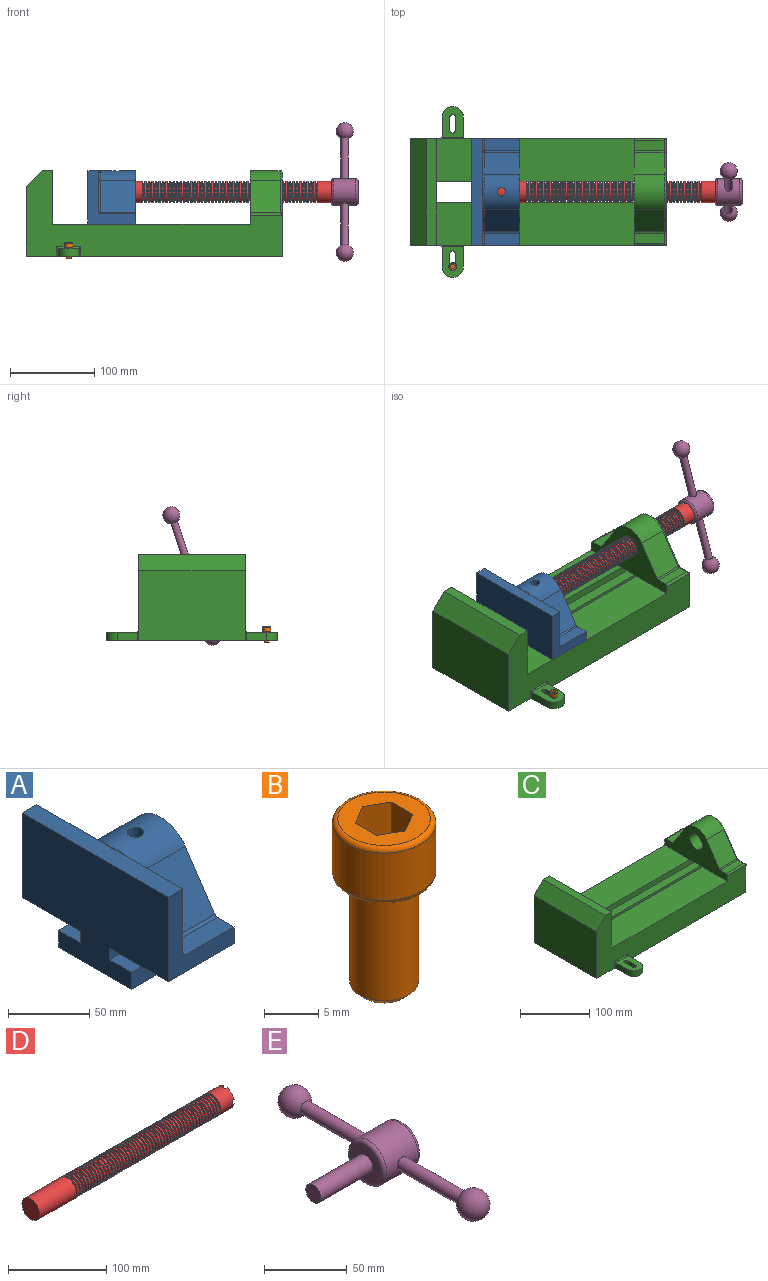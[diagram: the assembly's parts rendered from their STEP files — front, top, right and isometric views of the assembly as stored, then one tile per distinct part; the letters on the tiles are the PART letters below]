
ASSEMBLY  parts=5 mates=5
PART A: 36 faces, bbox 57.2x127x89 mm
  f0: plane 57.15x50.8mm, normal (0,0,-1), area 2903.2mm2, adj f6,f9,f10,f23
  f1: cylinder r=12.7mm len=44.45mm, axis (1,0,0), area 3464.3mm2, adj f6,f15,f16
  f2: plane 41.91x14.52mm, normal (0,0,1), area 608.5mm2, adj f6,f11,f24,f25
  f3: plane 51.86x48.26mm, normal (1,0,0), area 1495.7mm2, adj f8,f10,f31,f33,f35
  f4: plane 51.86x48.26mm, normal (1,0,0), area 1495.7mm2, adj f8,f11,f24,f28,f29
  f5: plane 57.15x50.8mm, normal (0,0,-1), area 2903.2mm2, adj f6,f9,f11,f22
  f6: plane 127x85.09mm, normal (1,0,0), area 5190.6mm2, adj f0,f1,f2,f5,f7,f10,f11,f12
  f7: plane 41.91x14.52mm, normal (0,0,1), area 608.5mm2, adj f6,f10,f30,f31
  f8: plane 127x12.7mm, normal (0,0,1), area 1612.9mm2, adj f3,f4,f9,f10,f11,f26,f34
  f9: plane 127x85.09mm, normal (-1,0,0), area 9096.8mm2, adj f0,f5,f8,f10,f11,f17,f18,f19
  f10: plane 63.5x57.15mm, normal (0,-1,0), area 1372.3mm2, adj f0,f3,f6,f7,f8,f9,f31
  f11: plane 63.5x57.15mm, normal (0,1,0), area 1372.3mm2, adj f2,f4,f5,f6,f8,f9,f24
  f12: plane 41.91x38.43mm, normal (0,-0.83,0.56), area 1939.2mm2, adj f6,f13,f30,f33
  f13: cylinder r=25.4mm len=44.45mm, axis (1,0,0), area 2026.5mm2, adj f6,f12,f14,f16,f26,f28,f34,f35
  f14: plane 41.91x38.43mm, normal (0,0.83,0.56), area 1939.2mm2, adj f6,f13,f25,f29
  f15: plane 25.4x25.4mm, normal (1,0,0), area 506.7mm2, adj f1
  f16: cylinder r=5.08mm len=13.76mm, axis (0,0,1), area 414mm2, adj f1,f13
  f17: plane 57.15x19.05mm, normal (0,0,1), area 1088.7mm2, adj f6,f9,f18,f23
  f18: plane 57.15x12.7mm, normal (0,-1,0), area 725.8mm2, adj f6,f9,f17,f19
  f19: plane 63.5x57.15mm, normal (0,0,-1), area 3629mm2, adj f6,f9,f18,f20
  f20: plane 57.15x12.7mm, normal (0,1,0), area 725.8mm2, adj f6,f9,f19,f21
  f21: plane 57.15x19.05mm, normal (0,0,1), area 1088.7mm2, adj f6,f9,f20,f22
  f22: plane 57.15x8.89mm, normal (0,1,0), area 508.1mm2, adj f5,f6,f9,f21
  f23: plane 57.15x8.89mm, normal (0,-1,0), area 508.1mm2, adj f0,f6,f9,f17
  f24: cylinder r=2.54mm len=14.52mm, axis (0,-1,0), area 57.9mm2, adj f2,f4,f11,f27
  f25: cylinder r=2.54mm len=41.91mm, axis (1,0,0), area 104.3mm2, adj f2,f6,f14,f27
  f26: bspline ~12.24x2.8mm, area 20.9mm2, adj f8,f13,f28
  f27: sphere r=2.54mm, area 6.3mm2, adj f24,f25,f29
  f28: torus R=27.94mm, axis (1,0,0), area 57.8mm2, adj f4,f13,f26,f29
  f29: cylinder r=2.54mm len=39.84mm, axis (0,-0.56,0.83), area 184.6mm2, adj f4,f14,f27,f28
  f30: cylinder r=2.54mm len=41.91mm, axis (1,0,0), area 104.3mm2, adj f6,f7,f12,f32
  f31: cylinder r=2.54mm len=14.52mm, axis (0,-1,0), area 57.9mm2, adj f3,f7,f10,f32
  f32: sphere r=2.54mm, area 6.3mm2, adj f30,f31,f33
  f33: cylinder r=2.54mm len=39.84mm, axis (0,-0.56,-0.83), area 184.6mm2, adj f3,f12,f32,f35
  f34: bspline ~12.24x2.8mm, area 20.9mm2, adj f8,f13,f35
  f35: torus R=27.94mm, axis (1,0,0), area 57.8mm2, adj f3,f13,f33,f34
PART B: 15 faces, bbox 10.3x10.3x19.1 mm
  f0: plane 8.51x8.51mm, normal (0,0,1), area 37.2mm2, adj f5,f6,f7,f8,f9,f10,f14
  f1: cylinder r=3.17mm len=11.94mm, axis (0,0,1), area 238.2mm2, adj f4,f12
  f2: plane 4.83x4.83mm, normal (0,0,-1), area 18.3mm2, adj f12
  f3: cylinder r=4.76mm len=9.53mm, axis (0,0,-1), area 159.6mm2, adj f13,f14
  f4: plane 8.51x8.51mm, normal (0,0,-1), area 25.2mm2, adj f1,f13
  f5: plane 4.83x2.38mm, normal (-0.5,-0.87,0), area 13.3mm2, adj f0,f6,f10,f11
  f6: plane 4.83x2.38mm, normal (0.5,-0.87,0), area 13.3mm2, adj f0,f5,f7,f11
  f7: plane 4.83x2.75mm, normal (1,0,0), area 13.3mm2, adj f0,f6,f8,f11
  f8: plane 4.83x2.38mm, normal (0.5,0.87,0), area 13.3mm2, adj f0,f7,f9,f11
  f9: plane 4.83x2.38mm, normal (-0.5,0.87,0), area 13.3mm2, adj f0,f8,f10,f11
  f10: plane 4.83x2.75mm, normal (-1,0,0), area 13.3mm2, adj f0,f5,f9,f11
  f11: plane 5.5x4.76mm, normal (0,0,1), area 19.6mm2, adj f5,f6,f7,f8,f9,f10
  f12: cone r=3.17mm half-angle=45deg, axis (0,0,1), area 18.9mm2, adj f1,f2
  f13: torus R=4.25mm, axis (0,0,1), area 23mm2, adj f3,f4
  f14: torus R=4.25mm, axis (0,0,1), area 23mm2, adj f0,f3
PART C: 61 faces, bbox 304.8x203.2x103.7 mm
  f0: plane 304.8x101.6mm, normal (0,1,0), area 13520.3mm2, adj f3,f4,f5,f6,f7,f8,f9,f16
  f1: plane 304.8x101.6mm, normal (0,-1,0), area 13520.3mm2, adj f2,f3,f5,f6,f7,f8,f9,f16
  f2: plane 234.95x50.8mm, normal (0,0,1), area 11935.5mm2, adj f1,f5,f16,f26
  f3: plane 127x99.06mm, normal (1,0,0), area 7097.5mm2, adj f0,f1,f9,f14,f17,f18,f19,f20
  f4: plane 234.95x50.8mm, normal (0,0,1), area 11935.5mm2, adj f0,f5,f16,f27
  f5: plane 127x101.6mm, normal (1,0,0), area 9516.1mm2, adj f0,f1,f2,f4,f6,f9,f18,f19
  f6: plane 127x12.7mm, normal (0,0,1), area 1612.9mm2, adj f0,f1,f5,f7
  f7: plane 127x19.05mm, normal (-0.71,0,0.71), area 3421.5mm2, adj f0,f1,f6,f8
  f8: plane 127x82.55mm, normal (-1,0,0), area 10483.8mm2, adj f0,f1,f7,f9
  f9: plane 304.8x203.2mm, normal (0,0,-1), area 33298.3mm2, adj f0,f1,f3,f5,f8,f21,f22,f39
  f10: plane 35.56x11.98mm, normal (0,0,1), area 426mm2, adj f16,f28,f29,f30
  f11: plane 38.43x35.56mm, normal (0,0.83,0.56), area 1645.4mm2, adj f12,f16,f29,f32
  f12: cylinder r=25.4mm len=42.19mm, axis (1,0,0), area 1770.2mm2, adj f11,f13,f16,f33
  f13: plane 38.43x35.56mm, normal (0,-0.83,0.56), area 1645.4mm2, adj f12,f16,f34,f35
  f14: cylinder r=12.7mm len=38.1mm, axis (1,0,0), area 3040.2mm2, adj f3,f16
  f15: plane 35.56x11.98mm, normal (0,0,1), area 426mm2, adj f16,f34,f36,f38
  f16: plane 127x63.5mm, normal (-1,0,0), area 4155.5mm2, adj f0,f1,f2,f4,f10,f11,f12,f13
  f17: plane 38.1x25.4mm, normal (0,0,-1), area 967.7mm2, adj f3,f16,f26,f27
  f18: plane 273.05x19.05mm, normal (0,0,-1), area 5201.6mm2, adj f3,f5,f19,f26
  f19: plane 273.05x12.7mm, normal (0,1,0), area 3467.7mm2, adj f3,f5,f18,f20
  f20: plane 273.05x19.05mm, normal (0,0,1), area 5201.6mm2, adj f3,f5,f19,f21
  f21: plane 273.05x16.51mm, normal (0,1,0), area 4508.1mm2, adj f3,f5,f9,f20
  f22: plane 273.05x16.51mm, normal (0,-1,0), area 4508.1mm2, adj f3,f5,f9,f23
  f23: plane 273.05x19.05mm, normal (0,0,1), area 5201.6mm2, adj f3,f5,f22,f24
  f24: plane 273.05x12.7mm, normal (0,-1,0), area 3467.7mm2, adj f3,f5,f23,f25
  f25: plane 273.05x19.05mm, normal (0,0,-1), area 5201.6mm2, adj f3,f5,f24,f27
  f26: plane 273.05x8.89mm, normal (0,1,0), area 2427.4mm2, adj f2,f3,f5,f17,f18
  f27: plane 273.05x8.89mm, normal (0,-1,0), area 2427.4mm2, adj f3,f4,f5,f17,f25
  f28: cylinder r=2.54mm len=38.1mm, axis (1,0,0), area 148.3mm2, adj f0,f10,f16,f30
  f29: cylinder r=2.54mm len=35.56mm, axis (-1,0,0), area 88.5mm2, adj f10,f11,f16,f31
  f30: cylinder r=2.54mm len=14.52mm, axis (0,1,0), area 54.3mm2, adj f3,f10,f28,f31
  f31: torus R=5.08mm, axis (-1,0,0), area 13.5mm2, adj f3,f29,f30,f32
  f32: cylinder r=2.54mm len=39.84mm, axis (0,0.56,-0.83), area 184.6mm2, adj f3,f11,f31,f33
  f33: torus R=22.86mm, axis (-1,0,0), area 191.4mm2, adj f3,f12,f32,f35
  f34: cylinder r=2.54mm len=35.56mm, axis (-1,0,0), area 88.5mm2, adj f13,f15,f16,f37
  f35: cylinder r=2.54mm len=39.84mm, axis (0,0.56,0.83), area 184.6mm2, adj f3,f13,f33,f37
  f36: cylinder r=2.54mm len=38.1mm, axis (-1,0,0), area 148.3mm2, adj f1,f15,f16,f38
  f37: torus R=5.08mm, axis (-1,0,0), area 13.5mm2, adj f3,f34,f35,f38
  f38: cylinder r=2.54mm len=14.52mm, axis (0,1,0), area 54.3mm2, adj f3,f15,f36,f37
  f39: plane 23.88x9.53mm, normal (-1,0,0), area 227.4mm2, adj f9,f45,f46,f60
  f40: plane 23.88x9.53mm, normal (1,0,0), area 227.4mm2, adj f9,f45,f46,f58
  f41: cylinder r=3.3mm len=9.53mm, axis (0,0,-1), area 98.8mm2, adj f9,f42,f44,f46
  f42: plane 15.62x9.53mm, normal (-1,0,0), area 148.8mm2, adj f9,f41,f43,f46
  f43: cylinder r=3.3mm len=9.53mm, axis (0,0,-1), area 98.8mm2, adj f9,f42,f44,f46
  f44: plane 15.62x9.53mm, normal (1,0,0), area 148.8mm2, adj f9,f41,f43,f46
  f45: cylinder r=12.7mm len=25.4mm, axis (0,0,-1), area 380mm2, adj f9,f39,f40,f46
  f46: plane 36.58x25.4mm, normal (0,0,1), area 722.4mm2, adj f39,f40,f41,f42,f43,f44,f45,f59
  f47: plane 23.88x9.53mm, normal (-1,0,0), area 227.4mm2, adj f9,f53,f54,f56
  f48: plane 23.88x9.53mm, normal (1,0,0), area 227.4mm2, adj f9,f53,f54,f55
  f49: cylinder r=3.3mm len=9.53mm, axis (0,0,-1), area 98.8mm2, adj f9,f50,f52,f54
  f50: plane 15.62x9.53mm, normal (-1,0,0), area 148.8mm2, adj f9,f49,f51,f54
  f51: cylinder r=3.3mm len=9.53mm, axis (0,0,-1), area 98.8mm2, adj f9,f50,f52,f54
  f52: plane 15.62x9.53mm, normal (1,0,0), area 148.8mm2, adj f9,f49,f51,f54
  f53: cylinder r=12.7mm len=25.4mm, axis (0,0,-1), area 380mm2, adj f9,f47,f48,f54
  f54: plane 36.58x25.4mm, normal (0,0,1), area 722.4mm2, adj f47,f48,f49,f50,f51,f52,f53,f57
  f55: cylinder r=1.52mm len=11.05mm, axis (0,0,-1), area 24.1mm2, adj f0,f9,f48,f57
  f56: cylinder r=1.52mm len=11.05mm, axis (0,0,1), area 24.1mm2, adj f0,f9,f47,f57
  f57: cylinder r=1.52mm len=28.45mm, axis (1,0,0), area 63.5mm2, adj f0,f54,f55,f56
  f58: cylinder r=1.52mm len=11.05mm, axis (0,0,1), area 24.1mm2, adj f1,f9,f40,f59
  f59: cylinder r=1.52mm len=28.45mm, axis (-1,0,0), area 63.5mm2, adj f1,f46,f58,f60
  f60: cylinder r=1.52mm len=11.05mm, axis (0,0,-1), area 24.1mm2, adj f1,f9,f39,f59
PART D: 220 faces, bbox 279.4x25.4x25.4 mm
  f0: cylinder r=12.7mm len=25.4mm, axis (-1,0,0), area 1468.2mm2, adj f1,f2,f3,f5,f7,f208,f209,f210
  f1: plane 9.9x9.9mm, normal (1,0,0), area 62.3mm2, adj f0,f4,f213,f216
  f2: plane 9.9x9.9mm, normal (1,0,0), area 62.3mm2, adj f0,f4,f210,f218
  f3: plane 9.9x9.9mm, normal (1,0,0), area 62.3mm2, adj f0,f4,f209,f212
  f4: cylinder r=6.35mm len=25.4mm, axis (1,0,0), area 960.3mm2, adj f1,f2,f3,f5,f6,f208,f209,f210
  f5: plane 9.9x9.9mm, normal (1,0,0), area 62.3mm2, adj f0,f4,f215,f217
  f6: plane 12.7x12.7mm, normal (1,0,0), area 126.7mm2, adj f4
  f7: cone r=12.7mm half-angle=76deg, axis (1,0,0), area 188mm2, adj f0,f9
  f8: cone r=10.16mm half-angle=76deg, axis (-1,0,0), area 188mm2, adj f9,f10
  f9: cylinder r=10.16mm len=20.32mm, axis (1,0,0), area 81.1mm2, adj f7,f8
  f10: cylinder r=12.7mm len=25.4mm, axis (-1,0,0), area 131.7mm2, adj f8,f11
  f11: cone r=12.7mm half-angle=76deg, axis (1,0,0), area 188mm2, adj f10,f13
  f12: cone r=10.16mm half-angle=76deg, axis (-1,0,0), area 188mm2, adj f13,f14
  f13: cylinder r=10.16mm len=20.32mm, axis (1,0,0), area 81.1mm2, adj f11,f12
  f14: cylinder r=12.7mm len=25.4mm, axis (-1,0,0), area 131.7mm2, adj f12,f15
  f15: cone r=12.7mm half-angle=76deg, axis (1,0,0), area 188mm2, adj f14,f17
  f16: cone r=10.16mm half-angle=76deg, axis (-1,0,0), area 188mm2, adj f17,f18
  f17: cylinder r=10.16mm len=20.32mm, axis (1,0,0), area 81.1mm2, adj f15,f16
  f18: cylinder r=12.7mm len=25.4mm, axis (-1,0,0), area 131.7mm2, adj f16,f19
  f19: cone r=12.7mm half-angle=76deg, axis (1,0,0), area 188mm2, adj f18,f21
  f20: cone r=10.16mm half-angle=76deg, axis (-1,0,0), area 188mm2, adj f21,f22
  f21: cylinder r=10.16mm len=20.32mm, axis (1,0,0), area 81.1mm2, adj f19,f20
  f22: cylinder r=12.7mm len=25.4mm, axis (-1,0,0), area 131.7mm2, adj f20,f23
  f23: cone r=12.7mm half-angle=76deg, axis (1,0,0), area 188mm2, adj f22,f25
  f24: cone r=10.16mm half-angle=76deg, axis (-1,0,0), area 188mm2, adj f25,f26
  f25: cylinder r=10.16mm len=20.32mm, axis (1,0,0), area 81.1mm2, adj f23,f24
  f26: cylinder r=12.7mm len=25.4mm, axis (-1,0,0), area 131.7mm2, adj f24,f27
  f27: cone r=12.7mm half-angle=76deg, axis (1,0,0), area 188mm2, adj f26,f29
  f28: cone r=10.16mm half-angle=76deg, axis (-1,0,0), area 188mm2, adj f29,f30
  f29: cylinder r=10.16mm len=20.32mm, axis (1,0,0), area 81.1mm2, adj f27,f28
  f30: cylinder r=12.7mm len=25.4mm, axis (-1,0,0), area 131.7mm2, adj f28,f31
  f31: cone r=12.7mm half-angle=76deg, axis (1,0,0), area 188mm2, adj f30,f33
  f32: cone r=10.16mm half-angle=76deg, axis (-1,0,0), area 188mm2, adj f33,f34
  f33: cylinder r=10.16mm len=20.32mm, axis (1,0,0), area 81.1mm2, adj f31,f32
  f34: cylinder r=12.7mm len=25.4mm, axis (-1,0,0), area 131.7mm2, adj f32,f35
  f35: cone r=12.7mm half-angle=76deg, axis (1,0,0), area 188mm2, adj f34,f37
  f36: cone r=10.16mm half-angle=76deg, axis (-1,0,0), area 188mm2, adj f37,f38
  f37: cylinder r=10.16mm len=20.32mm, axis (1,0,0), area 81.1mm2, adj f35,f36
  f38: cylinder r=12.7mm len=25.4mm, axis (-1,0,0), area 131.7mm2, adj f36,f39
  f39: cone r=12.7mm half-angle=76deg, axis (1,0,0), area 188mm2, adj f38,f41
  f40: cone r=10.16mm half-angle=76deg, axis (-1,0,0), area 188mm2, adj f41,f42
  f41: cylinder r=10.16mm len=20.32mm, axis (1,0,0), area 81.1mm2, adj f39,f40
  f42: cylinder r=12.7mm len=25.4mm, axis (-1,0,0), area 131.7mm2, adj f40,f43
  f43: cone r=12.7mm half-angle=76deg, axis (1,0,0), area 188mm2, adj f42,f45
  f44: cone r=10.16mm half-angle=76deg, axis (-1,0,0), area 188mm2, adj f45,f46
  f45: cylinder r=10.16mm len=20.32mm, axis (1,0,0), area 81.1mm2, adj f43,f44
  f46: cylinder r=12.7mm len=25.4mm, axis (-1,0,0), area 131.7mm2, adj f44,f47
  f47: cone r=12.7mm half-angle=76deg, axis (1,0,0), area 188mm2, adj f46,f49
  f48: cone r=10.16mm half-angle=76deg, axis (-1,0,0), area 188mm2, adj f49,f50
  f49: cylinder r=10.16mm len=20.32mm, axis (1,0,0), area 81.1mm2, adj f47,f48
  f50: cylinder r=12.7mm len=25.4mm, axis (-1,0,0), area 131.7mm2, adj f48,f51
  f51: cone r=12.7mm half-angle=76deg, axis (1,0,0), area 188mm2, adj f50,f53
  f52: cone r=10.16mm half-angle=76deg, axis (-1,0,0), area 188mm2, adj f53,f54
  f53: cylinder r=10.16mm len=20.32mm, axis (1,0,0), area 81.1mm2, adj f51,f52
  f54: cylinder r=12.7mm len=25.4mm, axis (-1,0,0), area 131.7mm2, adj f52,f55
  f55: cone r=12.7mm half-angle=76deg, axis (1,0,0), area 188mm2, adj f54,f57
  f56: cone r=10.16mm half-angle=76deg, axis (-1,0,0), area 188mm2, adj f57,f58
  f57: cylinder r=10.16mm len=20.32mm, axis (1,0,0), area 81.1mm2, adj f55,f56
  f58: cylinder r=12.7mm len=25.4mm, axis (-1,0,0), area 131.7mm2, adj f56,f59
  f59: cone r=12.7mm half-angle=76deg, axis (1,0,0), area 188mm2, adj f58,f61
  f60: cone r=10.16mm half-angle=76deg, axis (-1,0,0), area 188mm2, adj f61,f62
  f61: cylinder r=10.16mm len=20.32mm, axis (1,0,0), area 81.1mm2, adj f59,f60
  f62: cylinder r=12.7mm len=25.4mm, axis (-1,0,0), area 131.7mm2, adj f60,f63
  f63: cone r=12.7mm half-angle=76deg, axis (1,0,0), area 188mm2, adj f62,f65
  f64: cone r=10.16mm half-angle=76deg, axis (-1,0,0), area 188mm2, adj f65,f66
  f65: cylinder r=10.16mm len=20.32mm, axis (1,0,0), area 81.1mm2, adj f63,f64
  f66: cylinder r=12.7mm len=25.4mm, axis (-1,0,0), area 131.7mm2, adj f64,f67
  f67: cone r=12.7mm half-angle=76deg, axis (1,0,0), area 188mm2, adj f66,f69
  f68: cone r=10.16mm half-angle=76deg, axis (-1,0,0), area 188mm2, adj f69,f70
  f69: cylinder r=10.16mm len=20.32mm, axis (1,0,0), area 81.1mm2, adj f67,f68
  f70: cylinder r=12.7mm len=25.4mm, axis (-1,0,0), area 131.7mm2, adj f68,f71
  f71: cone r=12.7mm half-angle=76deg, axis (1,0,0), area 188mm2, adj f70,f73
  f72: cone r=10.16mm half-angle=76deg, axis (-1,0,0), area 188mm2, adj f73,f74
  f73: cylinder r=10.16mm len=20.32mm, axis (1,0,0), area 81.1mm2, adj f71,f72
  f74: cylinder r=12.7mm len=25.4mm, axis (-1,0,0), area 131.7mm2, adj f72,f75
  f75: cone r=12.7mm half-angle=76deg, axis (1,0,0), area 188mm2, adj f74,f77
  f76: cone r=10.16mm half-angle=76deg, axis (-1,0,0), area 188mm2, adj f77,f78
  f77: cylinder r=10.16mm len=20.32mm, axis (1,0,0), area 81.1mm2, adj f75,f76
  f78: cylinder r=12.7mm len=25.4mm, axis (-1,0,0), area 131.7mm2, adj f76,f79
  f79: cone r=12.7mm half-angle=76deg, axis (1,0,0), area 188mm2, adj f78,f81
  f80: cone r=10.16mm half-angle=76deg, axis (-1,0,0), area 188mm2, adj f81,f82
  f81: cylinder r=10.16mm len=20.32mm, axis (1,0,0), area 81.1mm2, adj f79,f80
  f82: cylinder r=12.7mm len=25.4mm, axis (-1,0,0), area 131.7mm2, adj f80,f83
  f83: cone r=12.7mm half-angle=76deg, axis (1,0,0), area 188mm2, adj f82,f85
  f84: cone r=10.16mm half-angle=76deg, axis (-1,0,0), area 188mm2, adj f85,f86
  f85: cylinder r=10.16mm len=20.32mm, axis (1,0,0), area 81.1mm2, adj f83,f84
  f86: cylinder r=12.7mm len=25.4mm, axis (-1,0,0), area 131.7mm2, adj f84,f87
  f87: cone r=12.7mm half-angle=76deg, axis (1,0,0), area 188mm2, adj f86,f89
  f88: cone r=10.16mm half-angle=76deg, axis (-1,0,0), area 188mm2, adj f89,f90
  f89: cylinder r=10.16mm len=20.32mm, axis (1,0,0), area 81.1mm2, adj f87,f88
  f90: cylinder r=12.7mm len=25.4mm, axis (-1,0,0), area 131.7mm2, adj f88,f91
  f91: cone r=12.7mm half-angle=76deg, axis (1,0,0), area 188mm2, adj f90,f93
  f92: cone r=10.16mm half-angle=76deg, axis (-1,0,0), area 188mm2, adj f93,f94
  f93: cylinder r=10.16mm len=20.32mm, axis (1,0,0), area 81.1mm2, adj f91,f92
  f94: cylinder r=12.7mm len=25.4mm, axis (-1,0,0), area 131.7mm2, adj f92,f95
  f95: cone r=12.7mm half-angle=76deg, axis (1,0,0), area 188mm2, adj f94,f97
  f96: cone r=10.16mm half-angle=76deg, axis (-1,0,0), area 188mm2, adj f97,f98
  f97: cylinder r=10.16mm len=20.32mm, axis (1,0,0), area 81.1mm2, adj f95,f96
  f98: cylinder r=12.7mm len=25.4mm, axis (-1,0,0), area 131.7mm2, adj f96,f99
  f99: cone r=12.7mm half-angle=76deg, axis (1,0,0), area 188mm2, adj f98,f101
  f100: cone r=10.16mm half-angle=76deg, axis (-1,0,0), area 188mm2, adj f101,f102
  f101: cylinder r=10.16mm len=20.32mm, axis (1,0,0), area 81.1mm2, adj f99,f100
  f102: cylinder r=12.7mm len=25.4mm, axis (-1,0,0), area 131.7mm2, adj f100,f103
  f103: cone r=12.7mm half-angle=76deg, axis (1,0,0), area 188mm2, adj f102,f105
  f104: cone r=10.16mm half-angle=76deg, axis (-1,0,0), area 188mm2, adj f105,f106
  f105: cylinder r=10.16mm len=20.32mm, axis (1,0,0), area 81.1mm2, adj f103,f104
  f106: cylinder r=12.7mm len=25.4mm, axis (-1,0,0), area 131.7mm2, adj f104,f107
  f107: cone r=12.7mm half-angle=76deg, axis (1,0,0), area 188mm2, adj f106,f109
  f108: cone r=10.16mm half-angle=76deg, axis (-1,0,0), area 188mm2, adj f109,f110
  f109: cylinder r=10.16mm len=20.32mm, axis (1,0,0), area 81.1mm2, adj f107,f108
  f110: cylinder r=12.7mm len=25.4mm, axis (-1,0,0), area 131.7mm2, adj f108,f111
  f111: cone r=12.7mm half-angle=76deg, axis (1,0,0), area 188mm2, adj f110,f113
  f112: cone r=10.16mm half-angle=76deg, axis (-1,0,0), area 188mm2, adj f113,f114
  f113: cylinder r=10.16mm len=20.32mm, axis (1,0,0), area 81.1mm2, adj f111,f112
  f114: cylinder r=12.7mm len=25.4mm, axis (-1,0,0), area 131.7mm2, adj f112,f115
  f115: cone r=12.7mm half-angle=76deg, axis (1,0,0), area 188mm2, adj f114,f117
  f116: cone r=10.16mm half-angle=76deg, axis (-1,0,0), area 188mm2, adj f117,f118
  f117: cylinder r=10.16mm len=20.32mm, axis (1,0,0), area 81.1mm2, adj f115,f116
  f118: cylinder r=12.7mm len=25.4mm, axis (-1,0,0), area 131.7mm2, adj f116,f119
  f119: cone r=12.7mm half-angle=76deg, axis (1,0,0), area 188mm2, adj f118,f121
  f120: cone r=10.16mm half-angle=76deg, axis (-1,0,0), area 188mm2, adj f121,f122
  f121: cylinder r=10.16mm len=20.32mm, axis (1,0,0), area 81.1mm2, adj f119,f120
  f122: cylinder r=12.7mm len=25.4mm, axis (-1,0,0), area 131.7mm2, adj f120,f123
  f123: cone r=12.7mm half-angle=76deg, axis (1,0,0), area 188mm2, adj f122,f125
  f124: cone r=10.16mm half-angle=76deg, axis (-1,0,0), area 188mm2, adj f125,f126
  f125: cylinder r=10.16mm len=20.32mm, axis (1,0,0), area 81.1mm2, adj f123,f124
  f126: cylinder r=12.7mm len=25.4mm, axis (-1,0,0), area 131.7mm2, adj f124,f127
  f127: cone r=12.7mm half-angle=76deg, axis (1,0,0), area 188mm2, adj f126,f129
  f128: cone r=10.16mm half-angle=76deg, axis (-1,0,0), area 188mm2, adj f129,f130
  f129: cylinder r=10.16mm len=20.32mm, axis (1,0,0), area 81.1mm2, adj f127,f128
  f130: cylinder r=12.7mm len=25.4mm, axis (-1,0,0), area 131.7mm2, adj f128,f131
  f131: cone r=12.7mm half-angle=76deg, axis (1,0,0), area 188mm2, adj f130,f133
  f132: cone r=10.16mm half-angle=76deg, axis (-1,0,0), area 188mm2, adj f133,f134
  f133: cylinder r=10.16mm len=20.32mm, axis (1,0,0), area 81.1mm2, adj f131,f132
  f134: cylinder r=12.7mm len=25.4mm, axis (-1,0,0), area 131.7mm2, adj f132,f135
  f135: cone r=12.7mm half-angle=76deg, axis (1,0,0), area 188mm2, adj f134,f137
  f136: cone r=10.16mm half-angle=76deg, axis (-1,0,0), area 188mm2, adj f137,f138
  f137: cylinder r=10.16mm len=20.32mm, axis (1,0,0), area 81.1mm2, adj f135,f136
  f138: cylinder r=12.7mm len=25.4mm, axis (-1,0,0), area 131.7mm2, adj f136,f139
  f139: cone r=12.7mm half-angle=76deg, axis (1,0,0), area 188mm2, adj f138,f141
  f140: cone r=10.16mm half-angle=76deg, axis (-1,0,0), area 188mm2, adj f141,f142
  f141: cylinder r=10.16mm len=20.32mm, axis (1,0,0), area 81.1mm2, adj f139,f140
  f142: cylinder r=12.7mm len=25.4mm, axis (-1,0,0), area 131.7mm2, adj f140,f143
  f143: cone r=12.7mm half-angle=76deg, axis (1,0,0), area 188mm2, adj f142,f145
  f144: cone r=10.16mm half-angle=76deg, axis (-1,0,0), area 188mm2, adj f145,f146
  f145: cylinder r=10.16mm len=20.32mm, axis (1,0,0), area 81.1mm2, adj f143,f144
  f146: cylinder r=12.7mm len=25.4mm, axis (-1,0,0), area 131.7mm2, adj f144,f147
  f147: cone r=12.7mm half-angle=76deg, axis (1,0,0), area 188mm2, adj f146,f149
  f148: cone r=10.16mm half-angle=76deg, axis (-1,0,0), area 188mm2, adj f149,f150
  f149: cylinder r=10.16mm len=20.32mm, axis (1,0,0), area 81.1mm2, adj f147,f148
  f150: cylinder r=12.7mm len=25.4mm, axis (-1,0,0), area 131.7mm2, adj f148,f151
  f151: cone r=12.7mm half-angle=76deg, axis (1,0,0), area 188mm2, adj f150,f153
  f152: cone r=10.16mm half-angle=76deg, axis (-1,0,0), area 188mm2, adj f153,f154
  f153: cylinder r=10.16mm len=20.32mm, axis (1,0,0), area 81.1mm2, adj f151,f152
  f154: cylinder r=12.7mm len=25.4mm, axis (-1,0,0), area 131.7mm2, adj f152,f155
  f155: cone r=12.7mm half-angle=76deg, axis (1,0,0), area 188mm2, adj f154,f157
  f156: cone r=10.16mm half-angle=76deg, axis (-1,0,0), area 188mm2, adj f157,f158
  f157: cylinder r=10.16mm len=20.32mm, axis (1,0,0), area 81.1mm2, adj f155,f156
  f158: cylinder r=12.7mm len=25.4mm, axis (-1,0,0), area 131.7mm2, adj f156,f159
  f159: cone r=12.7mm half-angle=76deg, axis (1,0,0), area 188mm2, adj f158,f161
  f160: cone r=10.16mm half-angle=76deg, axis (-1,0,0), area 188mm2, adj f161,f162
  f161: cylinder r=10.16mm len=20.32mm, axis (1,0,0), area 81.1mm2, adj f159,f160
  f162: cylinder r=12.7mm len=25.4mm, axis (-1,0,0), area 131.7mm2, adj f160,f163
  f163: cone r=12.7mm half-angle=76deg, axis (1,0,0), area 188mm2, adj f162,f165
  f164: cone r=10.16mm half-angle=76deg, axis (-1,0,0), area 188mm2, adj f165,f166
  f165: cylinder r=10.16mm len=20.32mm, axis (1,0,0), area 81.1mm2, adj f163,f164
  f166: cylinder r=12.7mm len=25.4mm, axis (-1,0,0), area 131.7mm2, adj f164,f167
  f167: cone r=12.7mm half-angle=76deg, axis (1,0,0), area 188mm2, adj f166,f169
  f168: cone r=10.16mm half-angle=76deg, axis (-1,0,0), area 188mm2, adj f169,f170
  f169: cylinder r=10.16mm len=20.32mm, axis (1,0,0), area 81.1mm2, adj f167,f168
  f170: cylinder r=12.7mm len=25.4mm, axis (-1,0,0), area 131.7mm2, adj f168,f171
  f171: cone r=12.7mm half-angle=76deg, axis (1,0,0), area 188mm2, adj f170,f173
  f172: cone r=10.16mm half-angle=76deg, axis (-1,0,0), area 188mm2, adj f173,f174
  f173: cylinder r=10.16mm len=20.32mm, axis (1,0,0), area 81.1mm2, adj f171,f172
  f174: cylinder r=12.7mm len=25.4mm, axis (-1,0,0), area 131.7mm2, adj f172,f175
  f175: cone r=12.7mm half-angle=76deg, axis (1,0,0), area 188mm2, adj f174,f177
  f176: cone r=10.16mm half-angle=76deg, axis (-1,0,0), area 188mm2, adj f177,f178
  f177: cylinder r=10.16mm len=20.32mm, axis (1,0,0), area 81.1mm2, adj f175,f176
  f178: cylinder r=12.7mm len=25.4mm, axis (-1,0,0), area 131.7mm2, adj f176,f179
  f179: cone r=12.7mm half-angle=76deg, axis (1,0,0), area 188mm2, adj f178,f181
  f180: cone r=10.16mm half-angle=76deg, axis (-1,0,0), area 188mm2, adj f181,f182
  f181: cylinder r=10.16mm len=20.32mm, axis (1,0,0), area 81.1mm2, adj f179,f180
  f182: cylinder r=12.7mm len=25.4mm, axis (-1,0,0), area 131.7mm2, adj f180,f183
  f183: cone r=12.7mm half-angle=76deg, axis (1,0,0), area 188mm2, adj f182,f185
  f184: cone r=10.16mm half-angle=76deg, axis (-1,0,0), area 188mm2, adj f185,f186
  f185: cylinder r=10.16mm len=20.32mm, axis (1,0,0), area 81.1mm2, adj f183,f184
  f186: cylinder r=12.7mm len=25.4mm, axis (-1,0,0), area 131.7mm2, adj f184,f187
  f187: cone r=12.7mm half-angle=76deg, axis (1,0,0), area 188mm2, adj f186,f189
  f188: cone r=10.16mm half-angle=76deg, axis (-1,0,0), area 188mm2, adj f189,f190
  f189: cylinder r=10.16mm len=20.32mm, axis (1,0,0), area 81.1mm2, adj f187,f188
  f190: cylinder r=12.7mm len=25.4mm, axis (-1,0,0), area 131.7mm2, adj f188,f191
  f191: cone r=12.7mm half-angle=76deg, axis (1,0,0), area 188mm2, adj f190,f193
  f192: cone r=10.16mm half-angle=76deg, axis (-1,0,0), area 188mm2, adj f193,f194
  f193: cylinder r=10.16mm len=20.32mm, axis (1,0,0), area 81.1mm2, adj f191,f192
  f194: cylinder r=12.7mm len=25.4mm, axis (-1,0,0), area 131.7mm2, adj f192,f195
  f195: cone r=12.7mm half-angle=76deg, axis (1,0,0), area 188mm2, adj f194,f197
  f196: cone r=10.16mm half-angle=76deg, axis (-1,0,0), area 188mm2, adj f197,f198
  f197: cylinder r=10.16mm len=20.32mm, axis (1,0,0), area 81.1mm2, adj f195,f196
  f198: cylinder r=12.7mm len=25.4mm, axis (-1,0,0), area 131.7mm2, adj f196,f199
  f199: cone r=12.7mm half-angle=76deg, axis (1,0,0), area 188mm2, adj f198,f201
  f200: cone r=10.16mm half-angle=76deg, axis (-1,0,0), area 188mm2, adj f201,f202
  f201: cylinder r=10.16mm len=20.32mm, axis (1,0,0), area 81.1mm2, adj f199,f200
  f202: cylinder r=12.7mm len=25.4mm, axis (-1,0,0), area 131.7mm2, adj f200,f203
  f203: cone r=12.7mm half-angle=76deg, axis (1,0,0), area 188mm2, adj f202,f205
  f204: cone r=10.16mm half-angle=76deg, axis (-1,0,0), area 188mm2, adj f205,f207
  f205: cylinder r=10.16mm len=20.32mm, axis (1,0,0), area 81.1mm2, adj f203,f204
  f206: plane 25.4x25.4mm, normal (-1,0,0), area 506.7mm2, adj f207
  f207: cylinder r=12.7mm len=52.45mm, axis (-1,0,0), area 4185.4mm2, adj f204,f206
  f208: plane 6.88x5.08mm, normal (1,0,0), area 32.7mm2, adj f0,f4,f209,f210
  f209: plane 6.62x2.54mm, normal (0,-1,0), area 16.8mm2, adj f0,f3,f4,f208
  f210: plane 6.62x2.54mm, normal (0,1,0), area 16.8mm2, adj f0,f2,f4,f208
  f211: plane 6.88x5.08mm, normal (1,0,0), area 32.7mm2, adj f0,f4,f212,f213
  f212: plane 6.62x2.54mm, normal (0,0,1), area 16.8mm2, adj f0,f3,f4,f211
  f213: plane 6.62x2.54mm, normal (0,0,-1), area 16.8mm2, adj f0,f1,f4,f211
  f214: plane 6.88x5.08mm, normal (1,0,0), area 32.7mm2, adj f0,f4,f215,f216
  f215: plane 6.62x2.54mm, normal (0,1,0), area 16.8mm2, adj f0,f4,f5,f214
  f216: plane 6.62x2.54mm, normal (0,-1,0), area 16.8mm2, adj f0,f1,f4,f214
  f217: plane 6.62x2.54mm, normal (0,0,-1), area 16.8mm2, adj f0,f4,f5,f219
  f218: plane 6.62x2.54mm, normal (0,0,1), area 16.8mm2, adj f0,f2,f4,f219
  f219: plane 6.88x5.08mm, normal (1,0,0), area 32.7mm2, adj f0,f4,f217,f218
PART E: 11 faces, bbox 76.2x172.7x34.4 mm
  f0: sphere r=10.16mm, area 1231.8mm2, adj f1
  f1: cylinder r=4.45mm len=51.82mm, axis (0,1,0), area 1438.5mm2, adj f0,f4
  f2: sphere r=10.16mm, area 1231.8mm2, adj f3
  f3: cylinder r=4.45mm len=51.82mm, axis (0,1,0), area 1438.5mm2, adj f2,f4
  f4: cylinder r=15.88mm len=31.75mm, axis (-1,0,0), area 2534.7mm2, adj f1,f3,f9,f10
  f5: cylinder r=6.35mm len=44.45mm, axis (-1,0,0), area 1773.5mm2, adj f6,f8
  f6: plane 12.7x12.7mm, normal (-1,0,0), area 126.7mm2, adj f5
  f7: plane 26.67x26.67mm, normal (1,0,0), area 558.6mm2, adj f10
  f8: plane 26.67x26.67mm, normal (-1,0,0), area 432mm2, adj f5,f9
  f9: torus R=13.33mm, axis (1,0,0), area 374.8mm2, adj f4,f8
  f10: torus R=13.33mm, axis (1,0,0), area 374.8mm2, adj f4,f7
PLACE A t=(41.94,0,0)mm
PLACE B rot(axis=(0,0,1),90deg) t=(-254,-88.9,9.52)mm
PLACE C at identity fixed
PLACE D rot(axis=(1,0,0),71.2deg) t=(41.94,72.14,51.67)mm
PLACE E rot(axis=(1,0,0),71.2deg) t=(20.35,72.14,51.67)mm
MATE fastened D.f4 <-> E.f5  axis (1,0,0) through (58.45,0,76.2)mm
MATE planar A.f0 <-> C.f2  axis (0,0,-1) through (-202.54,-38.1,38.1)mm
MATE pin_slot B.f1 <-> C.f41  axis (0,0,1) through (-254,-88.9,9.52)mm
MATE revolute D.f7 <-> A.f28  axis (-1,0,0) through (-218.41,0,76.2)mm
MATE cylindrical C.f12 <-> D.f7  axis (-1,0,0) through (-38.1,0,76.2)mm
